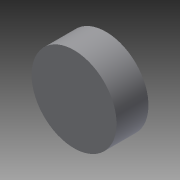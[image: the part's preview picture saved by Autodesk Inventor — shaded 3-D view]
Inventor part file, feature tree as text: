
AUTODESK INVENTOR PART (.ipt)
format: ipt  version: 2015 (Build 190159000, 159)  size: 83,456 bytes
history: native  units: mm
features: extrude x2, sketch x2
ambient origin geometry x8: Origin, YZ Plane, XZ Plane, XY Plane, X Axis, Y Axis, Z Axis, Center Point
bodies: Solid1 (feature_tree)
feature tree (4):
  extrude  "Extrusion1"  Depth=3.0mm TaperAngle=0.0deg
  extrude  "Extrusion2"  Depth=1.5mm
  sketch  "Sketch1"  dims[d0=8.0mm d1=3.0mm d2=0.0mm]
  sketch  "Sketch2"  dims[d3=3.19mm d4=1.595mm d6=1.595mm d7=1.5mm d8=0.0mm]
